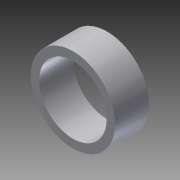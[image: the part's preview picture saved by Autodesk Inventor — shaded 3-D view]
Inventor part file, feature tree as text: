
AUTODESK INVENTOR PART (.ipt)
format: ipt  version: 2014 SP1 (Build 180222100, 222)  size: 83,968 bytes
history: native  units: in
note: dims shown in document units (in); Inventor stores cm internally (conversion verified against a paired STEP export)
features: extrude x1, sketch x1
ambient origin geometry x8: Origin, YZ Plane, XZ Plane, XY Plane, X Axis, Y Axis, Z Axis, Center Point
bodies: Solid1 (feature_tree)
feature tree (2):
  extrude  "Extrusion1"  Depth=0.253in
  sketch  "Sketch1"  dims[d0=0.5in d1=0.625in d2=0.253in d3=0.0in]
